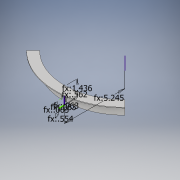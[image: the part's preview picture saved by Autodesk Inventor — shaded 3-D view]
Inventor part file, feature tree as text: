
AUTODESK INVENTOR PART (.ipt)
format: ipt  version: 2017 (Build 210142000, 142)  size: 192,000 bytes
history: native  units: in
note: dims shown in document units (in); Inventor stores cm internally (conversion verified against a paired STEP export)
features: sketch x6, extrude x5, revolve x2, plane x1
ambient origin geometry x8: Origin, YZ Plane, XZ Plane, XY Plane, X Axis, Y Axis, Z Axis, Center Point
bodies: Solid1 (feature_tree)
feature tree (14):
  revolve  "Revolution1"  [1 undecoded]
  plane  "Work Plane1"
  sketch  "Sketch2"  dims[d3=1.4364in d4=0.0625in]
  extrude  "Extrusion2"  Depth=0.0625in
  extrude  "Extrusion3"  TaperAngle=90.0deg  [1 undecoded]
  extrude  "Extrusion4"  Depth=0.375in
  extrude  "Extrusion5"  Depth=1.0in TaperAngle=0.0deg
  revolve  "Revolution2"  [1 undecoded]
  extrude  "Extrusion6"  Depth=0.25in
  sketch  "Sketch1"  dims[d1=0.5536in d2=0.0625in]
  sketch  "Sketch3"  dims[d5=0.0625in d6=90.0deg]
  sketch  "Sketch4"  dims[d7=0.562in d8=0.375in]
  sketch  "Sketch5"  dims[d11=0.3125in d12=1.0in d13=0.0in]
  sketch  "Sketch6"  dims[d14=0.0156in d15=0.0in d16=0.25in d17=0.0625in d18=0.0in d19=135.0deg d20=0.0in d21=0.0in d23=0.0312in d24=0.25in d25=0.25in d27=0.562in d28=90.0deg d29=1.0in d30=0.0in]
note: 3 required parameter values undecoded (feature->parameter linkage not recoverable at this tier; creation-order binding heuristic only, values carry confidence <= 0.55)